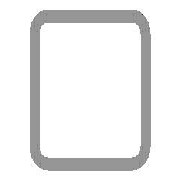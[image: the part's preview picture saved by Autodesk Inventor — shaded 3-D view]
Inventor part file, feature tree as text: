
AUTODESK INVENTOR PART (.ipt)
format: ipt  version: 2025.1 (Build 291241020, 241B)  size: 133,120 bytes
history: native  units: mm (DEFAULTED — no unit token found)
features: other x3, sketch x1, plane x1
ambient origin geometry x8: Origin, YZ Plane, XZ Plane, XY Plane, X Axis, Y Axis, Z Axis, Center Point
bodies: Solid1 (feature_tree), Body (feature_tree)
feature tree (5):
  other  "Driven Length"
  other  "Start plane"
  other  "End plane"
  sketch  "Sketch3"  dims[d3=1600.0mm d4=0.0mm d7=4.5mm d10=50.0mm d11=50.0mm d12=3.0mm d13=-0.0mm d14=1600.0mm d15=25.0mm d16=25.0mm d17=90.0deg d18=1600.0mm]
  plane  "Work Plane3"
